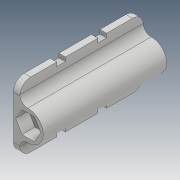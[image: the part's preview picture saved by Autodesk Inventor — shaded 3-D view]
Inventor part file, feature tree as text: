
AUTODESK INVENTOR PART (.ipt)
format: ipt  version: 2017 (Build 210142000, 142)  size: 155,136 bytes
history: native  units: mm
features: extrude x3, sketch x3, other x1, fillet x1
ambient origin geometry x8: Origin, YZ Plane, XZ Plane, XY Plane, X Axis, Y Axis, Z Axis, Center Point
bodies: Body1 (feature_tree)
feature tree (8):
  other  "Sólido1"
  extrude  "Extrusión1"  Depth=10.2mm
  extrude  "Extrusión2"  Depth=3.0mm
  extrude  "Extrusión3"  Depth=10.0mm
  fillet  "Empalme1"  Radius=6.0mm
  sketch  "Boceto1"  dims[d0=6.3mm d3=10.2mm]
  sketch  "Boceto2"  dims[d4=1.0mm d5=3.0mm]
  sketch  "Boceto4"  dims[d6=57.0mm d7=0.0mm d8=10.0mm d9=6.0mm d10=0.0mm d12=30.0mm d13=2.0mm d14=4.0mm d15=15.0mm d16=6.0mm d17=0.0mm d18=5.0mm]
